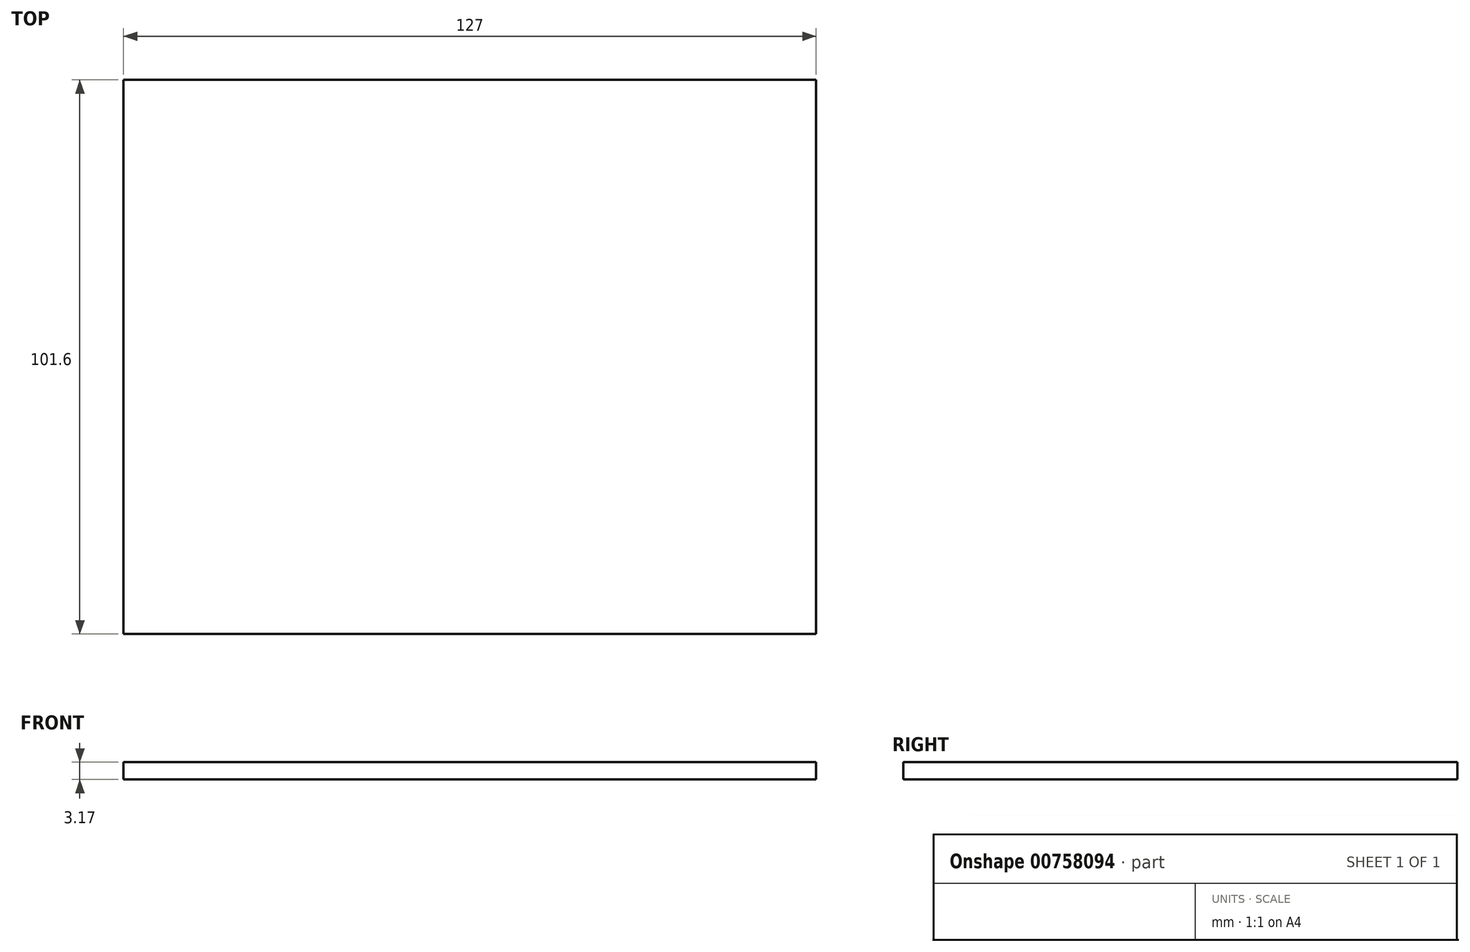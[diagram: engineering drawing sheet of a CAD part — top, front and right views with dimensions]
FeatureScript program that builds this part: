
annotation { "Feature Type Name" : "Feature", "Feature Type Description" : "" }
export const myFeature = defineFeature(function(context is Context, id is Id, definition is map)
    precondition{}
    {
        {
            var Q0;
            Q0=qCreatedBy(makeId("Top.planeOp"),FACE);
            var sketch = newSketch(context, id + "F0", { "sketchPlane" : qUnion([Q0])});
            skLineSegment(sketch, "E0.bottom", {"start": v(0, 0) * mm, "end": v(-127, 0) * mm});
            skLineSegment(sketch, "E0.top", {"start": v(0, 101.6) * mm, "end": v(-127, 101.6) * mm});
            skLineSegment(sketch, "E0.left", {"start": v(0, 0) * mm, "end": v(0, 101.6) * mm});
            skLineSegment(sketch, "E0.right", {"start": v(-127, 0) * mm, "end": v(-127, 101.6) * mm});
            skLineSegment(sketch, "E1", {"start": v(-127, 101.6) * mm, "end": v(-160.12, 81.23) * mm});
            skLineSegment(sketch, "E2", {"start": v(-160.12, 81.23) * mm, "end": v(-127, 61.38) * mm});
            skSolve(sketch);
        }
        {
            var Q0;
            {var subQ1=sQuery(id+"F0.wireOp",EDGE,"E0.bottom");Q0=makeQuery(id+"F0.imprint","IMPRINT",FACE,{"disambiguationData":[TD([[makeQuery(id+"F0.imprint","IMPRINT",EDGE,{"derivedFrom":subQ1}),-1.0]])]});}
            extrude(context, id + "F1", {"entities" : qUnion([Q0]), "depth" : 3.17 * mm, "offsetDistance" : 25.4 * mm});
        }
    });
